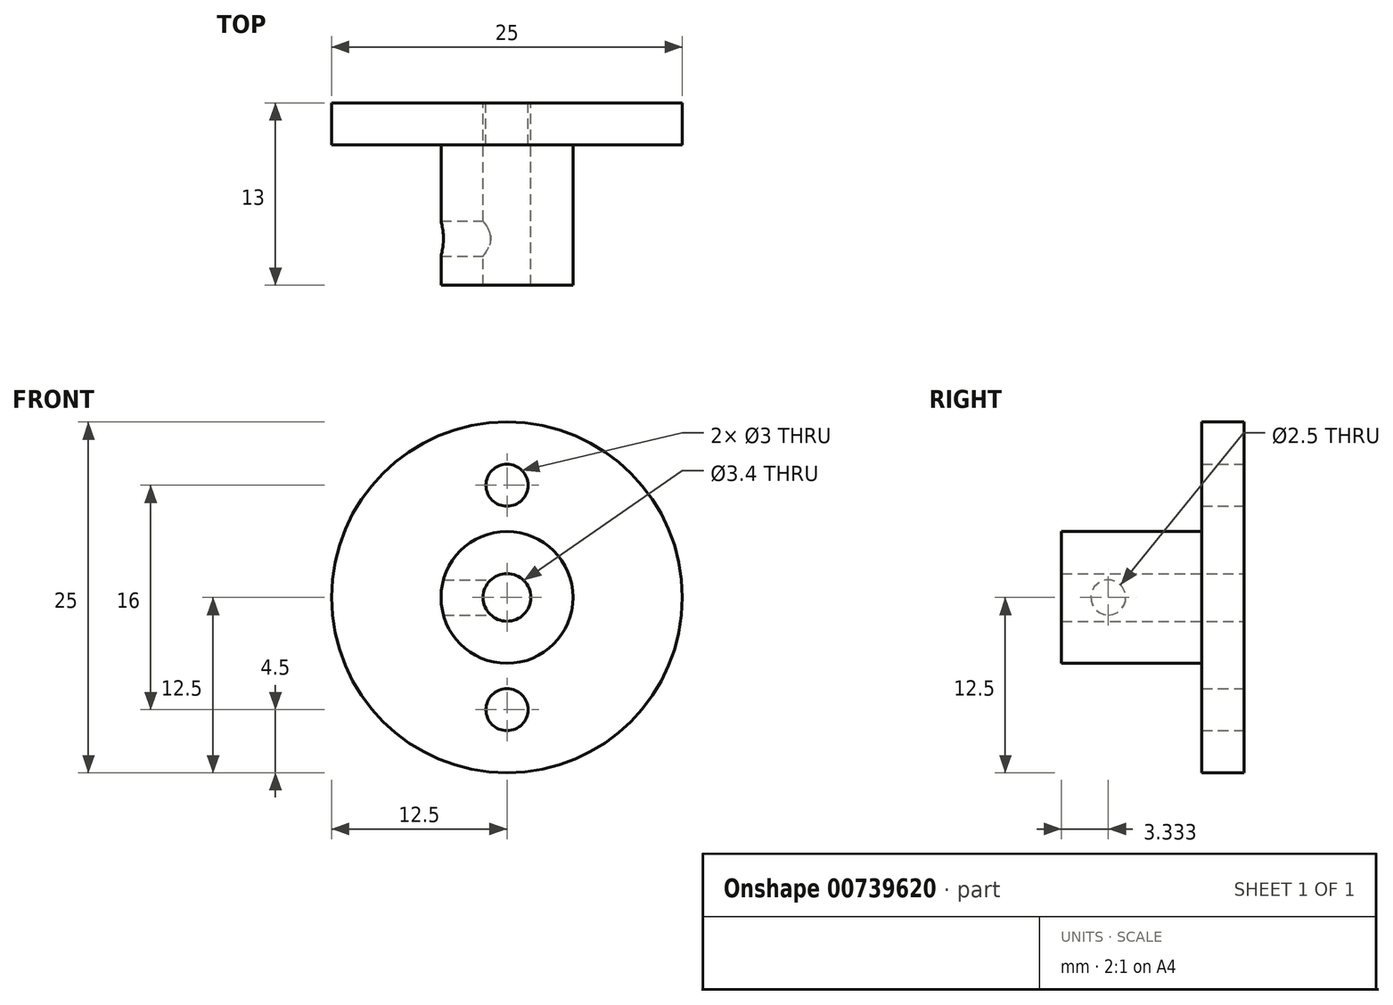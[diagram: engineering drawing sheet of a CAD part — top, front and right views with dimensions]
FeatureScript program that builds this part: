
annotation { "Feature Type Name" : "Feature", "Feature Type Description" : "" }
export const myFeature = defineFeature(function(context is Context, id is Id, definition is map)
    precondition{}
    {
        {
            assignVariable(context, id + "F0", {"name" : "setScrewExtrude", "anyValue" : 10 * mm});
        }
        {
            assignVariable(context, id + "F1", {"name" : "rivetExtrude", "anyValue" : 3 * mm});
        }
        {
            var Q0;
            Q0=qCreatedBy(makeId("Front.planeOp"),FACE);
            var sketch = newSketch(context, id + "F2", { "sketchPlane" : qUnion([Q0])});
            skCircle(sketch, "E0", {"center": v(0, 0) * mm, "radius": 12.5 * mm});
            skCircle(sketch, "E1", {"center": v(0, 0) * mm, "radius": 1.7 * mm});
            skCircle(sketch, "E2", {"center": v(0, 8) * mm, "radius": 1.5 * mm});
            skCircle(sketch, "E3", {"center": v(0, -8) * mm, "radius": 1.5 * mm});
            skSolve(sketch);
        }
        {
            var Q0;
            Q0=qSketchRegion(id+"F2",true);
            extrude(context, id + "F3", {"entities" : qUnion([Q0]), "depth" : getVariable(context, 'rivetExtrude'), "offsetDistance" : 25 * mm});
        }
        {
            var Q0;
            Q0=makeQuery(id+"F3.opExtrude","CAP_FACE",FACE,{"disambiguationData":[OSD([sQuery(id+"F2.wireOp",EDGE,"E0"),sQuery(id+"F2.wireOp",EDGE,"E1"),sQuery(id+"F2.wireOp",EDGE,"E2"),sQuery(id+"F2.wireOp",EDGE,"E3")])],"isStart":false});
            var sketch = newSketch(context, id + "F4", { "sketchPlane" : qUnion([Q0])});
            skCircle(sketch, "E4", {"center": v(0, 0) * mm, "radius": 1.7 * mm});
            skCircle(sketch, "E5", {"center": v(0, 0) * mm, "radius": 4.7 * mm});
            skSolve(sketch);
        }
        {
            var Q0;
            Q0=qSketchRegion(id+"F4",true);
            extrude(context, id + "F5", {"entities" : qUnion([Q0]), "operationType" : NewBodyOperationType.ADD, "depth" : getVariable(context, 'setScrewExtrude'), "offsetDistance" : 25 * mm});
        }
        {
            var Q0;
            Q0=qCreatedBy(makeId("Right.planeOp"),FACE);
            var sketch = newSketch(context, id + "F6", { "sketchPlane" : qUnion([Q0])});
            skCircle(sketch, "E6", {"center": v(-9.67, 0) * mm, "radius": 1.25 * mm});
            skSolve(sketch);
        }
        {
            var Q0;
            Q0=qSketchRegion(id+"F6",true);
            extrude(context, id + "F7", {"entities" : qUnion([Q0]), "operationType" : NewBodyOperationType.REMOVE, "oppositeDirection" : true, "depth" : 25 * mm, "offsetDistance" : 25 * mm});
        }
    });
